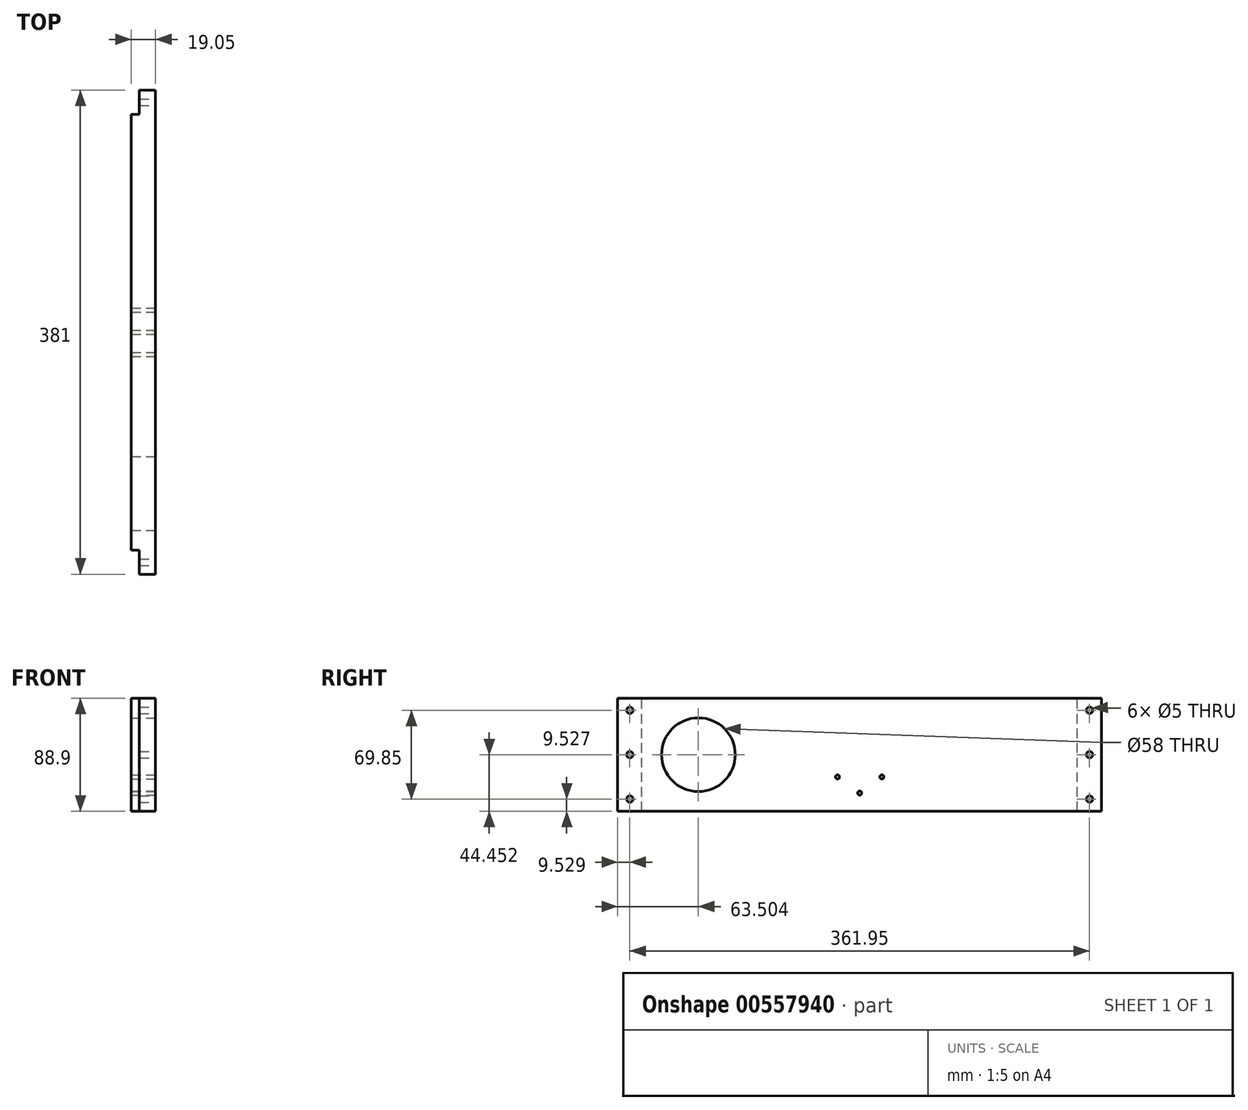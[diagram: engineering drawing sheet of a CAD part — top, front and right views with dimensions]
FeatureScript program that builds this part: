
annotation { "Feature Type Name" : "Feature", "Feature Type Description" : "" }
export const myFeature = defineFeature(function(context is Context, id is Id, definition is map)
    precondition{}
    {
        {
            var Q0;
            Q0=qCreatedBy(makeId("Right.planeOp"),FACE);
            var sketch = newSketch(context, id + "F0", { "sketchPlane" : qUnion([Q0])});
            skLineSegment(sketch, "E0.bottom", {"start": v(407.92, 24.9) * mm, "end": v(26.92, 24.9) * mm});
            skLineSegment(sketch, "E0.top", {"start": v(407.92, 113.8) * mm, "end": v(26.92, 113.8) * mm});
            skLineSegment(sketch, "E0.left", {"start": v(388.87, 24.9) * mm, "end": v(388.87, 113.8) * mm});
            skLineSegment(sketch, "E0.right", {"start": v(45.97, 24.9) * mm, "end": v(45.97, 113.8) * mm});
            skPoint(sketch, "E0.middle", {"position": v(217.42, 69.34) * mm});
            skLineSegment(sketch, "E1", {"start": v(26.92, 113.8) * mm, "end": v(26.92, 24.9) * mm});
            skLineSegment(sketch, "E2", {"start": v(407.92, 113.8) * mm, "end": v(407.92, 24.9) * mm});
            skCircle(sketch, "E3.MirrorC", {"center": v(398.4, 104.27) * mm, "radius": 2.5 * mm});
            skCircle(sketch, "E4.MirrorC", {"center": v(398.4, 34.42) * mm, "radius": 2.5 * mm});
            skCircle(sketch, "E5.MirrorC", {"center": v(398.4, 69.34) * mm, "radius": 2.5 * mm});
            skCircle(sketch, "E6.MirrorC", {"center": v(36.45, 104.27) * mm, "radius": 2.5 * mm});
            skCircle(sketch, "E7.MirrorC", {"center": v(36.45, 69.34) * mm, "radius": 2.5 * mm});
            skCircle(sketch, "E8.MirrorC", {"center": v(36.45, 34.42) * mm, "radius": 2.5 * mm});
            skCircle(sketch, "E9", {"center": v(90.42, 69.34) * mm, "radius": 29 * mm});
            skCircle(sketch, "E10", {"center": v(217.42, 39.18) * mm, "radius": 1.59 * mm});
            skCircle(sketch, "E11", {"center": v(234.89, 51.88) * mm, "radius": 1.59 * mm});
            skCircle(sketch, "E12", {"center": v(199.96, 51.88) * mm, "radius": 1.59 * mm});
            skSolve(sketch);
        }
        {
            var Q0;
            {var subQ0=sQuery(id+"F0.wireOp",EDGE,"E0.left");Q0=makeQuery(id+"F0.imprint","IMPRINT",FACE,{"disambiguationData":[TD([[makeQuery(id+"F0.imprint","IMPRINT",EDGE,{"derivedFrom":subQ0}),1.0]])]});}
            extrude(context, id + "F1", {"entities" : qUnion([Q0]), "depth" : -19.05 * mm, "offsetDistance" : 25.4 * mm});
        }
        {
            var Q0;
            {var subQ2=sQuery(id+"F0.wireOp",EDGE,"E0.right");Q0=makeQuery(id+"F0.imprint","IMPRINT",FACE,{"disambiguationData":[TD([[makeQuery(id+"F0.imprint","IMPRINT",EDGE,{"derivedFrom":subQ2}),1.0]])]});}
            var Q1;
            {var subQ2=sQuery(id+"F0.wireOp",EDGE,"E0.left");Q1=makeQuery(id+"F0.imprint","IMPRINT",FACE,{"disambiguationData":[TD([[makeQuery(id+"F0.imprint","IMPRINT",EDGE,{"derivedFrom":subQ2}),-1.0]])]});}
            extrude(context, id + "F2", {"entities" : qUnion([Q0, Q1]), "operationType" : NewBodyOperationType.ADD, "depth" : -12.7 * mm, "offsetDistance" : 25.4 * mm});
        }
    });
